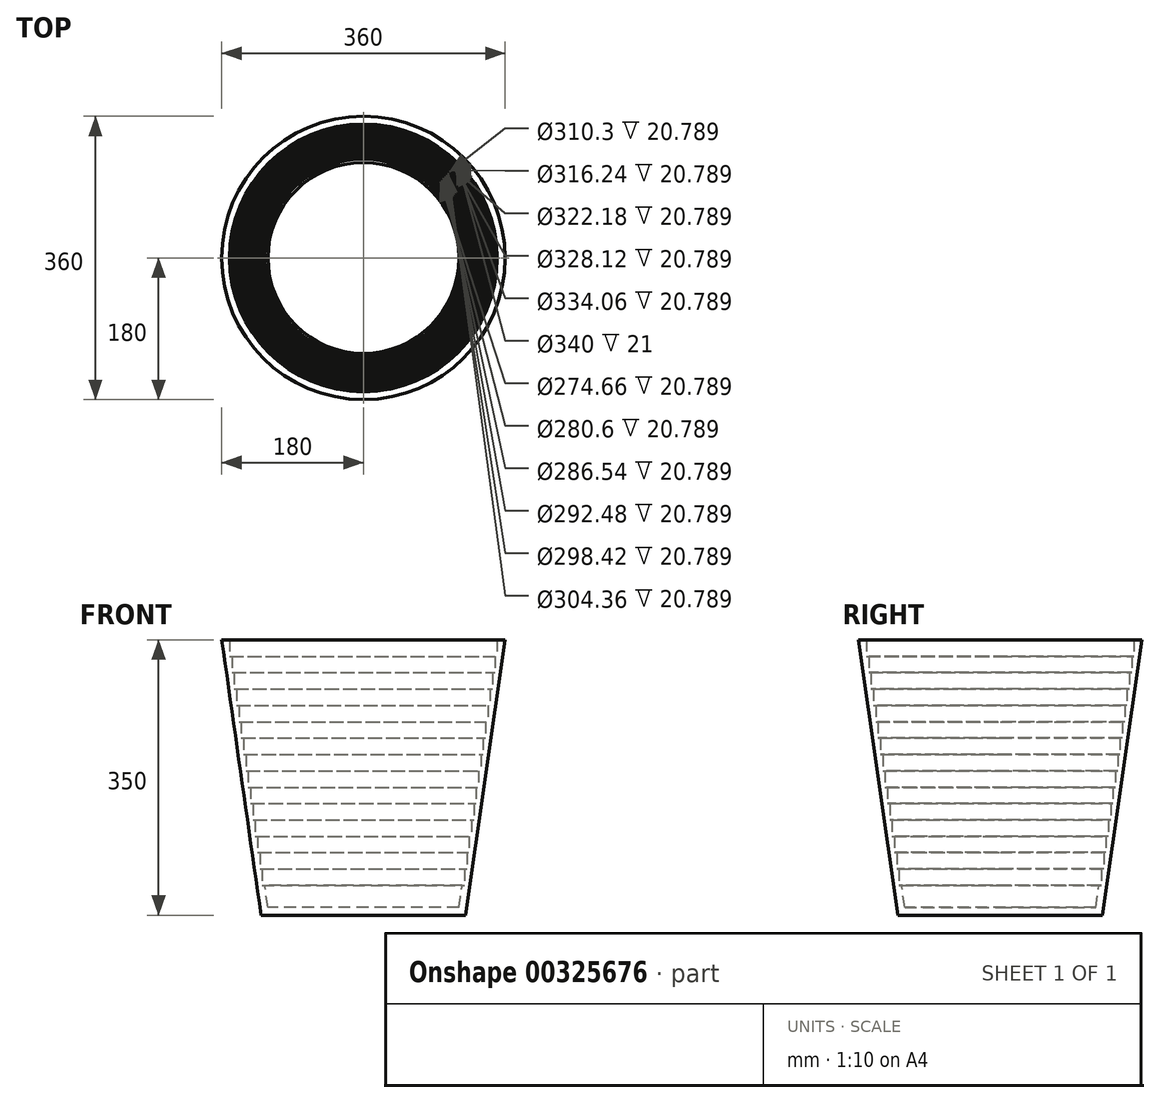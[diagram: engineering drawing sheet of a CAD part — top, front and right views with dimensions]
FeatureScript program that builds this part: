
annotation { "Feature Type Name" : "Feature", "Feature Type Description" : "" }
export const myFeature = defineFeature(function(context is Context, id is Id, definition is map)
    precondition{}
    {
        {
            var Q0;
            Q0=qCreatedBy(makeId("Front.planeOp"),FACE);
            var sketch = newSketch(context, id + "F0", { "sketchPlane" : qUnion([Q0])});
            skLineSegment(sketch, "E0", {"start": v(0, 350) * mm, "end": v(180, 350) * mm});
            skLineSegment(sketch, "E1", {"start": v(180, 350) * mm, "end": v(130, 0) * mm});
            skLineSegment(sketch, "E2", {"start": v(130, 0) * mm, "end": v(0, 0) * mm});
            skLineSegment(sketch, "E3", {"start": v(0, 0) * mm, "end": v(0, 350) * mm});
            skSolve(sketch);
        }
        {
            var Q0;
            Q0=makeQuery(id+"F0.imprint","IMPRINT",FACE,{"disambiguationData":[TD([[makeQuery(id+"F0.imprint","IMPRINT",EDGE,{"derivedFrom":sQuery(id+"F0.wireOp",EDGE,"E0")}),-1.0]])]});
            var Q1;
            Q1=sQuery(id+"F0.wireOp",EDGE,"E3");
            revolve(context, id + "F1", {"entities" : qUnion([Q0]), "axis" : qUnion([Q1]), "revolveType" : RevolveType.FULL});
        }
        {
            var Q0;
            Q0=makeQuery(id+"F1.opRevolve","SWEPT_FACE",FACE,{"disambiguationData":[OSD([sQuery(id+"F0.wireOp",EDGE,"E0")])]});
            shell(context, id + "F2", {"entities" : qUnion([Q0]), "thickness" : 10 * mm});
        }
        {
            var Q0;
            Q0=makeQuery(id+"F0.imprint","IMPRINT",FACE,{"disambiguationData":[TD([[makeQuery(id+"F0.imprint","IMPRINT",EDGE,{"derivedFrom":sQuery(id+"F0.wireOp",EDGE,"E0")}),-1.0]])]});
            var sketch = newSketch(context, id + "F3", { "sketchPlane" : qUnion([Q0])});
            skLineSegment(sketch, "E4", {"start": v(120, 0) * mm, "end": v(130, 0) * mm, "construction": true});
            skLineSegment(sketch, "E5", {"start": v(130, 0) * mm, "end": v(180, 350) * mm, "construction": true});
            skLineSegment(sketch, "E6", {"start": v(180, 350) * mm, "end": v(170, 350) * mm, "construction": true});
            skLineSegment(sketch, "E7", {"start": v(170, 350) * mm, "end": v(170, 329) * mm});
            skLineSegment(sketch, "E8", {"start": v(170, 329) * mm, "end": v(167, 329) * mm});
            skLineSegment(sketch, "E9.direction1", {"start": v(167, 329) * mm, "end": v(167, 329) * mm});
            skLineSegment(sketch, "E9.direction2", {"start": v(167, 329) * mm, "end": v(164.03, 308.21) * mm, "construction": true});
            skLineSegment(sketch, "E10.0.0.1", {"start": v(167.03, 329.21) * mm, "end": v(167.03, 308.21) * mm});
            skLineSegment(sketch, "E10.3.0.1", {"start": v(167.03, 308.21) * mm, "end": v(164.03, 308.21) * mm});
            skLineSegment(sketch, "E10.0.0.2", {"start": v(164.06, 308.42) * mm, "end": v(164.06, 287.42) * mm});
            skLineSegment(sketch, "E10.3.0.2", {"start": v(164.06, 287.42) * mm, "end": v(161.06, 287.42) * mm});
            skLineSegment(sketch, "E10.0.0.3", {"start": v(161.1, 287.63) * mm, "end": v(161.1, 266.63) * mm});
            skLineSegment(sketch, "E10.3.0.3", {"start": v(161.1, 266.63) * mm, "end": v(158.1, 266.63) * mm});
            skLineSegment(sketch, "E10.0.0.4", {"start": v(158.12, 266.84) * mm, "end": v(158.12, 245.84) * mm});
            skLineSegment(sketch, "E10.3.0.4", {"start": v(158.12, 245.84) * mm, "end": v(155.12, 245.84) * mm});
            skLineSegment(sketch, "E10.0.0.5", {"start": v(155.15, 246.06) * mm, "end": v(155.15, 225.06) * mm});
            skLineSegment(sketch, "E10.3.0.5", {"start": v(155.15, 225.06) * mm, "end": v(152.15, 225.06) * mm});
            skLineSegment(sketch, "E10.0.0.6", {"start": v(152.18, 225.27) * mm, "end": v(152.18, 204.27) * mm});
            skLineSegment(sketch, "E10.3.0.6", {"start": v(152.18, 204.27) * mm, "end": v(149.18, 204.27) * mm});
            skLineSegment(sketch, "E10.0.0.7", {"start": v(149.21, 204.48) * mm, "end": v(149.21, 183.48) * mm});
            skLineSegment(sketch, "E10.3.0.7", {"start": v(149.21, 183.48) * mm, "end": v(146.21, 183.48) * mm});
            skLineSegment(sketch, "E10.0.0.8", {"start": v(146.24, 183.69) * mm, "end": v(146.24, 162.69) * mm});
            skLineSegment(sketch, "E10.3.0.8", {"start": v(146.24, 162.69) * mm, "end": v(143.24, 162.69) * mm});
            skLineSegment(sketch, "E10.0.0.9", {"start": v(143.27, 162.9) * mm, "end": v(143.27, 141.9) * mm});
            skLineSegment(sketch, "E10.3.0.9", {"start": v(143.27, 141.9) * mm, "end": v(140.27, 141.9) * mm});
            skLineSegment(sketch, "E11.0.0.10", {"start": v(140.3, 142.11) * mm, "end": v(140.3, 121.11) * mm});
            skLineSegment(sketch, "E11.3.0.10", {"start": v(140.3, 121.11) * mm, "end": v(137.3, 121.11) * mm});
            skLineSegment(sketch, "E12.0.0.11", {"start": v(137.33, 121.32) * mm, "end": v(137.33, 100.32) * mm});
            skLineSegment(sketch, "E12.3.0.11", {"start": v(137.33, 100.32) * mm, "end": v(134.33, 100.32) * mm});
            skLineSegment(sketch, "E12.0.0.12", {"start": v(134.36, 100.53) * mm, "end": v(134.36, 79.53) * mm});
            skLineSegment(sketch, "E12.3.0.12", {"start": v(134.36, 79.53) * mm, "end": v(131.36, 79.53) * mm});
            skLineSegment(sketch, "E12.0.0.13", {"start": v(131.4, 79.74) * mm, "end": v(131.4, 58.74) * mm});
            skLineSegment(sketch, "E12.3.0.13", {"start": v(131.4, 58.74) * mm, "end": v(128.4, 58.74) * mm});
            skLineSegment(sketch, "E12.0.0.14", {"start": v(128.42, 58.95) * mm, "end": v(128.42, 37.95) * mm});
            skLineSegment(sketch, "E12.3.0.14", {"start": v(128.42, 37.95) * mm, "end": v(125.42, 37.95) * mm});
            skLineSegment(sketch, "E13", {"start": v(0, 349.66) * mm, "end": v(170, 350) * mm});
            skLineSegment(sketch, "E14", {"start": v(125.42, 37.95) * mm, "end": v(0, 37.95) * mm});
            skLineSegment(sketch, "E15", {"start": v(0, 37.95) * mm, "end": v(0, 349.66) * mm});
            skSolve(sketch);
        }
        {
            var Q0;
            Q0 = qSketchRegion(id + "F3", true);
            var Q1;
            Q1=sQuery(id+"F0.wireOp",EDGE,"E3");
            revolve(context, id + "F4", {"entities" : qUnion([Q0]), "axis" : qUnion([Q1]), "revolveType" : RevolveType.FULL});
        }
        {
            var Q0;
            Q0=makeQuery(id+"F4.opRevolve","SWEPT_BODY",BODY,{"disambiguationData":[OSD([sQuery(id+"F3.wireOp",EDGE,"vz75T0As-ydNs-ZXHa-mKhs-WrH59qLY2IUX"),sQuery(id+"F3.wireOp",EDGE,"E7"),sQuery(id+"F3.wireOp",EDGE,"E8"),sQuery(id+"F3.wireOp",EDGE,"E10.0.0.1"),sQuery(id+"F3.wireOp",EDGE,"E10.3.0.1"),sQuery(id+"F3.wireOp",EDGE,"E10.0.0.2"),sQuery(id+"F3.wireOp",EDGE,"E10.3.0.2"),sQuery(id+"F3.wireOp",EDGE,"E10.0.0.3"),sQuery(id+"F3.wireOp",EDGE,"E10.3.0.3"),sQuery(id+"F3.wireOp",EDGE,"E10.0.0.4"),sQuery(id+"F3.wireOp",EDGE,"E10.3.0.4"),sQuery(id+"F3.wireOp",EDGE,"E10.0.0.5"),sQuery(id+"F3.wireOp",EDGE,"E10.3.0.5"),sQuery(id+"F3.wireOp",EDGE,"E10.0.0.6"),sQuery(id+"F3.wireOp",EDGE,"E10.3.0.6"),sQuery(id+"F3.wireOp",EDGE,"E10.0.0.7"),sQuery(id+"F3.wireOp",EDGE,"E10.3.0.7"),sQuery(id+"F3.wireOp",EDGE,"E10.0.0.8"),sQuery(id+"F3.wireOp",EDGE,"E10.3.0.8"),sQuery(id+"F3.wireOp",EDGE,"E10.0.0.9"),sQuery(id+"F3.wireOp",EDGE,"E10.3.0.9"),sQuery(id+"F3.wireOp",EDGE,"E11.0.0.10"),sQuery(id+"F3.wireOp",EDGE,"E11.3.0.10"),sQuery(id+"F3.wireOp",EDGE,"E12.0.0.11"),sQuery(id+"F3.wireOp",EDGE,"E12.3.0.11"),sQuery(id+"F3.wireOp",EDGE,"E12.0.0.12"),sQuery(id+"F3.wireOp",EDGE,"E12.3.0.12"),sQuery(id+"F3.wireOp",EDGE,"E12.0.0.13"),sQuery(id+"F3.wireOp",EDGE,"E12.3.0.13"),sQuery(id+"F3.wireOp",EDGE,"E12.0.0.14"),sQuery(id+"F3.wireOp",EDGE,"E12.3.0.14")])]});
            var Q1;
            Q1=makeQuery(id+"F1.opRevolve","SWEPT_BODY",BODY,{"disambiguationData":[OSD([sQuery(id+"F0.wireOp",EDGE,"E0"),sQuery(id+"F0.wireOp",EDGE,"E1"),sQuery(id+"F0.wireOp",EDGE,"E2"),sQuery(id+"F0.wireOp",EDGE,"E3")])]});
            booleanBodies(context, id + "F5", {"operationType" : BooleanOperationType.SUBTRACTION, "tools" : qUnion([Q0]), "targets" : qUnion([Q1])});
        }
    });
